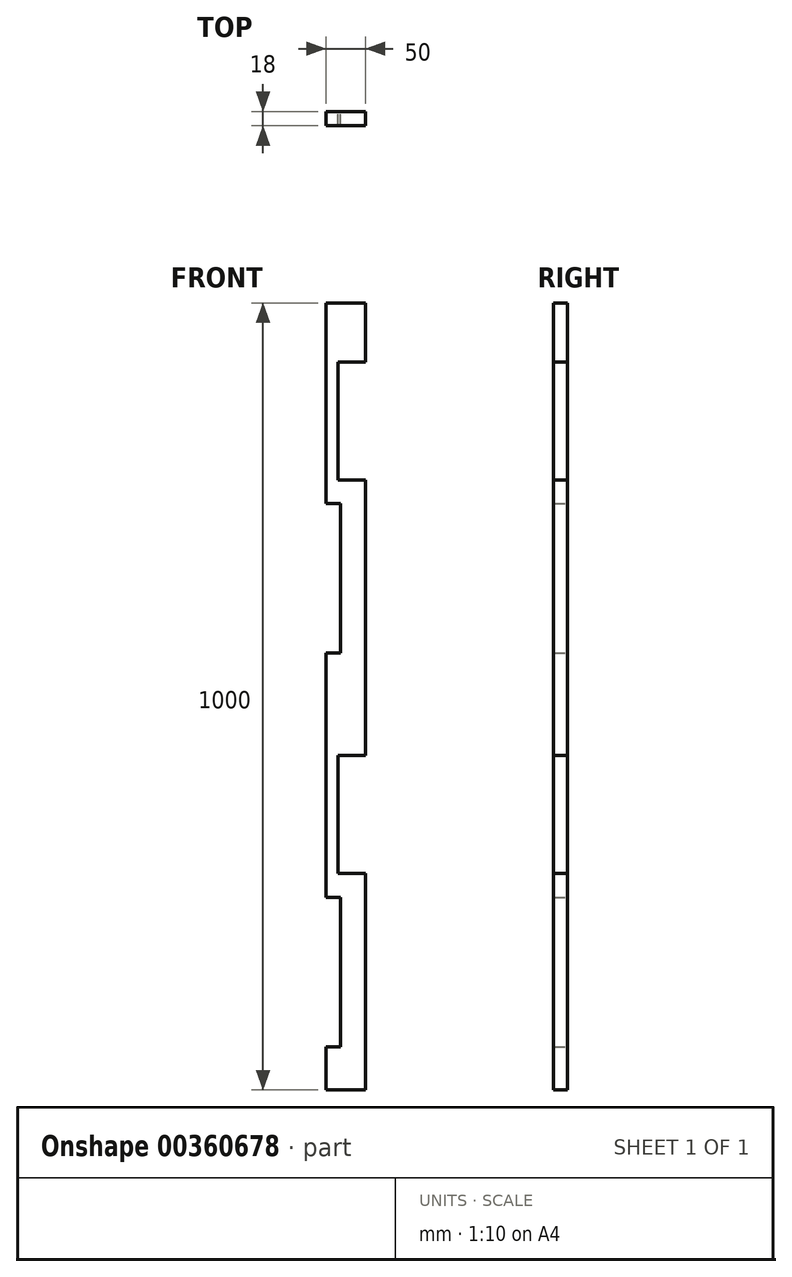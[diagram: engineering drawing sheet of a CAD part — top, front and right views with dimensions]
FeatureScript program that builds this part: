
annotation { "Feature Type Name" : "Feature", "Feature Type Description" : "" }
export const myFeature = defineFeature(function(context is Context, id is Id, definition is map)
    precondition{}
    {
        {
            var Q0;
            Q0=qCreatedBy(makeId("Front.planeOp"),FACE);
            var sketch = newSketch(context, id + "F0", { "sketchPlane" : qUnion([Q0])});
            skLineSegment(sketch, "E0.bottom", {"start": v(0, 0) * mm, "end": v(50, 0) * mm});
            skLineSegment(sketch, "E0.top", {"start": v(0, 1000) * mm, "end": v(50, 1000) * mm});
            skLineSegment(sketch, "E0.right", {"start": v(50, 0) * mm, "end": v(50, 275) * mm});
            skLineSegment(sketch, "E1.bottom", {"start": v(50, 275) * mm, "end": v(15, 275) * mm});
            skLineSegment(sketch, "E1.top", {"start": v(50, 425) * mm, "end": v(15, 425) * mm});
            skLineSegment(sketch, "E1.right", {"start": v(15, 275) * mm, "end": v(15, 425) * mm});
            skLineSegment(sketch, "E2.bottom", {"start": v(50, 925) * mm, "end": v(15, 925) * mm});
            skLineSegment(sketch, "E2.top", {"start": v(50, 775) * mm, "end": v(15, 775) * mm});
            skLineSegment(sketch, "E2.right", {"start": v(15, 925) * mm, "end": v(15, 775) * mm});
            skLineSegment(sketch, "E3.trimOffspring", {"start": v(50, 925) * mm, "end": v(50, 1000) * mm});
            skLineSegment(sketch, "E4.trimOffspring", {"start": v(50, 425) * mm, "end": v(50, 775) * mm});
            skLineSegment(sketch, "E5", {"start": v(0, 0) * mm, "end": v(0, 55) * mm});
            skLineSegment(sketch, "E6.bottom", {"start": v(0, 745) * mm, "end": v(18, 745) * mm});
            skLineSegment(sketch, "E6.top", {"start": v(0, 555) * mm, "end": v(18, 555) * mm});
            skLineSegment(sketch, "E6.right", {"start": v(18, 745) * mm, "end": v(18, 555) * mm});
            skLineSegment(sketch, "E7.bottom", {"start": v(0, 245) * mm, "end": v(18, 245) * mm});
            skLineSegment(sketch, "E7.top", {"start": v(0, 55) * mm, "end": v(18, 55) * mm});
            skLineSegment(sketch, "E7.right", {"start": v(18, 245) * mm, "end": v(18, 55) * mm});
            skLineSegment(sketch, "E8.trimOffspring", {"start": v(0, 745) * mm, "end": v(0, 1000) * mm});
            skLineSegment(sketch, "E9.trimOffspring", {"start": v(0, 245) * mm, "end": v(0, 555) * mm});
            skSolve(sketch);
        }
        {
            var Q0;
            Q0=makeQuery(id+"F0.imprint","IMPRINT",FACE,{"disambiguationData":[TD([[makeQuery(id+"F0.imprint","IMPRINT",EDGE,{"derivedFrom":sQuery(id+"F0.wireOp",EDGE,"E0.bottom")}),1.0]])]});
            extrude(context, id + "F1", {"entities" : qUnion([Q0]), "depth" : 18 * mm});
        }
    });
